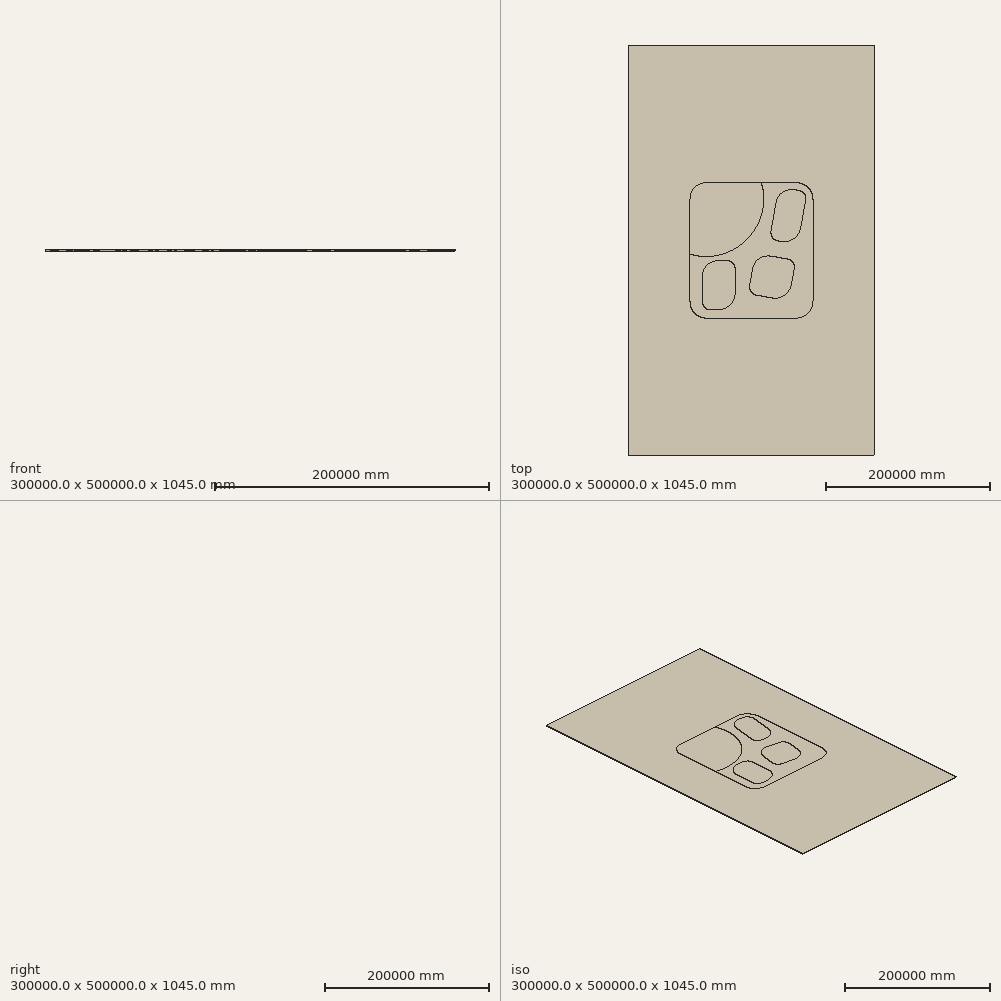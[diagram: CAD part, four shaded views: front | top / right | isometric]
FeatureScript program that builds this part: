
annotation { "Feature Type Name" : "Feature", "Feature Type Description" : "" }
export const myFeature = defineFeature(function(context is Context, id is Id, definition is map)
    precondition{}
    {
        {
            assignVariable(context, id + "F0", {"name" : "building1_height", "anyValue" : 15});
        }
        {
            assignVariable(context, id + "F1", {"name" : "building1_orient", "anyValue" : 0});
        }
        {
            assignVariable(context, id + "F2", {"name" : "building2_height", "anyValue" : 30});
        }
        {
            assignVariable(context, id + "F3", {"name" : "building2_orient", "anyValue" : 10});
        }
        {
            assignVariable(context, id + "F4", {"name" : "building3_height", "anyValue" : 45});
        }
        {
            assignVariable(context, id + "F5", {"name" : "building3_orient", "anyValue" : 10});
        }
        {
            var Q0;
            Q0=qCreatedBy(makeId("Top.planeOp"),FACE);
            var sketch = newSketch(context, id + "F6", { "sketchPlane" : qUnion([Q0])});
            skLineSegment(sketch, "E0.bottom", {"start": v(-55000, 82500) * mm, "end": v(55000, 82500) * mm});
            skLineSegment(sketch, "E0.top", {"start": v(-55000, -82500) * mm, "end": v(55000, -82500) * mm});
            skLineSegment(sketch, "E0.left", {"start": v(-75000, 62500) * mm, "end": v(-75000, -62500) * mm});
            skLineSegment(sketch, "E0.right", {"start": v(75000, 62500) * mm, "end": v(75000, -62500) * mm});
            skPoint(sketch, "E0.middle", {"position": v(0, 0) * mm});
            skLineSegment(sketch, "E1.bottom", {"start": v(-40000, -12500) * mm, "end": v(-30000, -12500) * mm});
            skLineSegment(sketch, "E1.top", {"start": v(-50000, -72500) * mm, "end": v(-40000, -72500) * mm});
            skLineSegment(sketch, "E1.left", {"start": v(-60000, -32500) * mm, "end": v(-60000, -62500) * mm});
            skLineSegment(sketch, "E1.right", {"start": v(-20000, -22500) * mm, "end": v(-20000, -52500) * mm});
            skPoint(sketch, "E1.middle", {"position": v(-40000, -42500) * mm});
            skPoint(sketch, "E1.cornerSnap0", {"position": v(-60000, -47500) * mm});
            skPoint(sketch, "E2.visualSharp", {"position": v(-60000, -12500) * mm});
            skArc(sketch, "E2.filletArc", {"start": v(-40000, -12500) * mm, "mid": v(-54142.14, -18357.86) * mm, "end": v(-60000, -32500) * mm});
            skPoint(sketch, "E3.visualSharp", {"position": v(-20000, -72500) * mm});
            skArc(sketch, "E3.filletArc", {"start": v(-40000, -72500) * mm, "mid": v(-25857.86, -66642.14) * mm, "end": v(-20000, -52500) * mm});
            skPoint(sketch, "E4.visualSharp", {"position": v(-20000, -12500) * mm});
            skArc(sketch, "E4.filletArc", {"start": v(-20000, -22500) * mm, "mid": v(-22928.93, -15428.93) * mm, "end": v(-30000, -12500) * mm});
            skPoint(sketch, "E5.visualSharp", {"position": v(-60000, -72500) * mm});
            skArc(sketch, "E5.filletArc", {"start": v(-60000, -62500) * mm, "mid": v(-57071.07, -69571.07) * mm, "end": v(-50000, -72500) * mm});
            skLineSegment(sketch, "E6.bottom", {"start": v(-75000, -82500) * mm, "end": v(-40000, -82500) * mm, "construction": true});
            skLineSegment(sketch, "E6.top", {"start": v(-75000, -42500) * mm, "end": v(-40000, -42500) * mm, "construction": true});
            skLineSegment(sketch, "E6.left", {"start": v(-75000, -82500) * mm, "end": v(-75000, -42500) * mm, "construction": true});
            skLineSegment(sketch, "E6.right", {"start": v(-40000, -82500) * mm, "end": v(-40000, -42500) * mm, "construction": true});
            skLineSegment(sketch, "E7.bottom", {"start": v(-75000, -82500) * mm, "end": v(25000, -82500) * mm});
            skLineSegment(sketch, "E7.top", {"start": v(-75000, -32500) * mm, "end": v(25000, -32500) * mm, "construction": true});
            skLineSegment(sketch, "E7.left", {"start": v(-75000, -82500) * mm, "end": v(-75000, -32500) * mm});
            skLineSegment(sketch, "E7.right", {"start": v(25000, -82500) * mm, "end": v(25000, -32500) * mm, "construction": true});
            skLineSegment(sketch, "E8.bottom", {"start": v(20000, -7500) * mm, "end": v(40000, -7500) * mm});
            skLineSegment(sketch, "E8.top", {"start": v(10000, -57500) * mm, "end": v(30000, -57500) * mm});
            skLineSegment(sketch, "E8.left", {"start": v(0, -27500) * mm, "end": v(0, -47500) * mm});
            skLineSegment(sketch, "E8.right", {"start": v(50000, -17500) * mm, "end": v(50000, -37500) * mm});
            skPoint(sketch, "E8.middle", {"position": v(25000, -32500) * mm});
            skPoint(sketch, "E9.visualSharp", {"position": v(0, -7500) * mm});
            skArc(sketch, "E9.filletArc", {"start": v(20000, -7500) * mm, "mid": v(5857.86, -13357.86) * mm, "end": v(0, -27500) * mm});
            skPoint(sketch, "E10.visualSharp", {"position": v(50000, -7500) * mm});
            skArc(sketch, "E10.filletArc", {"start": v(50000, -17500) * mm, "mid": v(47071.07, -10428.93) * mm, "end": v(40000, -7500) * mm});
            skPoint(sketch, "E11.visualSharp", {"position": v(50000, -57500) * mm});
            skArc(sketch, "E11.filletArc", {"start": v(30000, -57500) * mm, "mid": v(44142.14, -51642.14) * mm, "end": v(50000, -37500) * mm});
            skPoint(sketch, "E12.visualSharp", {"position": v(0, -57500) * mm});
            skArc(sketch, "E12.filletArc", {"start": v(0, -47500) * mm, "mid": v(2928.93, -54571.07) * mm, "end": v(10000, -57500) * mm});
            skLineSegment(sketch, "E13.bottom", {"start": v(-75000, -82500) * mm, "end": v(45000, -82500) * mm});
            skLineSegment(sketch, "E13.top", {"start": v(-75000, 42500) * mm, "end": v(45000, 42500) * mm, "construction": true});
            skLineSegment(sketch, "E13.left", {"start": v(-75000, -82500) * mm, "end": v(-75000, 42500) * mm});
            skLineSegment(sketch, "E13.right", {"start": v(45000, -82500) * mm, "end": v(45000, 42500) * mm, "construction": true});
            skLineSegment(sketch, "E14.bottom", {"start": v(47500, 75000) * mm, "end": v(52500, 75000) * mm});
            skLineSegment(sketch, "E14.top", {"start": v(37500, 10000) * mm, "end": v(42500, 10000) * mm});
            skLineSegment(sketch, "E14.left", {"start": v(27500, 55000) * mm, "end": v(27500, 20000) * mm});
            skLineSegment(sketch, "E14.right", {"start": v(62500, 65000) * mm, "end": v(62500, 30000) * mm});
            skPoint(sketch, "E14.middle", {"position": v(45000, 42500) * mm});
            skPoint(sketch, "E15.visualSharp", {"position": v(27500, 75000) * mm});
            skArc(sketch, "E15.filletArc", {"start": v(47500, 75000) * mm, "mid": v(33357.86, 69142.14) * mm, "end": v(27500, 55000) * mm});
            skPoint(sketch, "E16.visualSharp", {"position": v(62500, 75000) * mm});
            skArc(sketch, "E16.filletArc", {"start": v(62500, 65000) * mm, "mid": v(59571.07, 72071.07) * mm, "end": v(52500, 75000) * mm});
            skPoint(sketch, "E17.visualSharp", {"position": v(62500, 10000) * mm});
            skArc(sketch, "E17.filletArc", {"start": v(42500, 10000) * mm, "mid": v(56642.14, 15857.86) * mm, "end": v(62500, 30000) * mm});
            skPoint(sketch, "E18.visualSharp", {"position": v(27500, 10000) * mm});
            skArc(sketch, "E18.filletArc", {"start": v(27500, 20000) * mm, "mid": v(30428.93, 12928.93) * mm, "end": v(37500, 10000) * mm});
            skPoint(sketch, "E19.visualSharp", {"position": v(-75000, -82500) * mm});
            skArc(sketch, "E19.filletArc", {"start": v(-75000, -62500) * mm, "mid": v(-69142.14, -76642.14) * mm, "end": v(-55000, -82500) * mm});
            skPoint(sketch, "E20.visualSharp", {"position": v(75000, -82500) * mm});
            skArc(sketch, "E20.filletArc", {"start": v(55000, -82500) * mm, "mid": v(69142.14, -76642.14) * mm, "end": v(75000, -62500) * mm});
            skPoint(sketch, "E21.visualSharp", {"position": v(75000, 82500) * mm});
            skArc(sketch, "E21.filletArc", {"start": v(75000, 62500) * mm, "mid": v(69142.14, 76642.14) * mm, "end": v(55000, 82500) * mm});
            skPoint(sketch, "E22.visualSharp", {"position": v(-75000, 82500) * mm});
            skArc(sketch, "E22.filletArc", {"start": v(-55000, 82500) * mm, "mid": v(-69142.14, 76642.14) * mm, "end": v(-75000, 62500) * mm});
            skArc(sketch, "E23", {"start": v(12082.04, 82500) * mm, "mid": v(-5502.53, 13002.53) * mm, "end": v(-75000, -4582.04) * mm});
            skSolve(sketch);
        }
        {
            var Q0;
            Q0=makeQuery(id+"F6.imprint","IMPRINT",FACE,{"disambiguationData":[TD([[makeQuery(id+"F6.imprint","IMPRINT",EDGE,{"derivedFrom":sQuery(id+"F6.wireOp",EDGE,"E1.bottom")}),-1.0]])]});
            extrude(context, id + "F7", {"entities" : qUnion([Q0]), "depth" : (getVariable(context, 'building1_height')) * mm, "offsetDistance" : 25 * mm});
        }
        {
            var Q0;
            Q0=makeQuery(id+"F6.imprint","IMPRINT",FACE,{"disambiguationData":[TD([[makeQuery(id+"F6.imprint","IMPRINT",EDGE,{"derivedFrom":sQuery(id+"F6.wireOp",EDGE,"E8.bottom")}),-1.0]])]});
            extrude(context, id + "F8", {"entities" : qUnion([Q0]), "depth" : (getVariable(context, 'building2_height')) * mm, "offsetDistance" : 25 * mm});
        }
        {
            var Q0;
            Q0=makeQuery(id+"F6.imprint","IMPRINT",FACE,{"disambiguationData":[TD([[makeQuery(id+"F6.imprint","IMPRINT",EDGE,{"derivedFrom":sQuery(id+"F6.wireOp",EDGE,"E14.bottom")}),-1.0]])]});
            extrude(context, id + "F9", {"entities" : qUnion([Q0]), "depth" : (getVariable(context, 'building3_height')) * mm, "offsetDistance" : 25 * mm});
        }
        {
            var Q0;
            {var subQ1=sQuery(id+"F6.wireOp",EDGE,"E0.top");Q0=makeQuery(id+"F6.imprint","IMPRINT",FACE,{"disambiguationData":[TD([[makeQuery(id+"F6.imprint","IMPRINT",EDGE,{"derivedFrom":subQ1}),1.0]])]});}
            var Q1;
            Q1=makeQuery(id+"F6.imprint","IMPRINT",FACE,{"disambiguationData":[TD([[makeQuery(id+"F6.imprint","IMPRINT",EDGE,{"derivedFrom":sQuery(id+"F6.wireOp",EDGE,"E8.bottom")}),-1.0]])]});
            var Q2;
            Q2=makeQuery(id+"F6.imprint","IMPRINT",FACE,{"disambiguationData":[TD([[makeQuery(id+"F6.imprint","IMPRINT",EDGE,{"derivedFrom":sQuery(id+"F6.wireOp",EDGE,"E14.bottom")}),-1.0]])]});
            var Q3;
            Q3=makeQuery(id+"F6.imprint","IMPRINT",FACE,{"disambiguationData":[TD([[makeQuery(id+"F6.imprint","IMPRINT",EDGE,{"derivedFrom":sQuery(id+"F6.wireOp",EDGE,"E1.bottom")}),-1.0]])]});
            extrude(context, id + "F10", {"entities" : qUnion([Q0, Q1, Q2, Q3]), "oppositeDirection" : true, "depth" : 1000 * mm, "offsetDistance" : 25 * mm});
        }
        {
            var Q0;
            {var subQ1=sQuery(id+"F6.wireOp",EDGE,"E0.left");Q0=makeQuery(id+"F6.imprint","IMPRINT",FACE,{"disambiguationData":[TD([[makeQuery(id+"F6.imprint","IMPRINT",EDGE,{"derivedFrom":subQ1}),1.0]])]});}
            extrude(context, id + "F11", {"entities" : qUnion([Q0]), "oppositeDirection" : true, "depth" : 1000 * mm, "offsetDistance" : 25 * mm});
        }
        {
            var Q0;
            Q0=sQuery(id+"F6.wireOp",EDGE,"E6.top");
            cPlane(context, id + "F12", {"entities" : qUnion([Q0]), "cplaneType" : CPlaneType.LINE_ANGLE, "offset" : 25 * mm, "angle" : 0 * degree, "width" : 150 * mm, "height" : 150 * mm});
        }
        {
            var Q0;
            Q0=sQuery(id+"F6.wireOp",EDGE,"E7.top");
            cPlane(context, id + "F13", {"entities" : qUnion([Q0]), "cplaneType" : CPlaneType.LINE_ANGLE, "offset" : 25 * mm, "angle" : 0 * degree, "width" : 150 * mm, "height" : 150 * mm});
        }
        {
            var Q0;
            Q0=sQuery(id+"F6.wireOp",EDGE,"E13.top");
            cPlane(context, id + "F14", {"entities" : qUnion([Q0]), "cplaneType" : CPlaneType.LINE_ANGLE, "offset" : 25 * mm, "angle" : 0 * degree, "width" : 150 * mm, "height" : 150 * mm});
        }
        {
            var Q0;
            Q0=qCreatedBy(id+"F12.planeOp",FACE);
            var sketch = newSketch(context, id + "F15", { "sketchPlane" : qUnion([Q0])});
            skLineSegment(sketch, "E24", {"start": v(40000, 0) * mm, "end": v(40000, 15000) * mm});
            skSolve(sketch);
        }
        {
            var Q0;
            Q0=qCreatedBy(id+"F13.planeOp",FACE);
            var sketch = newSketch(context, id + "F16", { "sketchPlane" : qUnion([Q0])});
            skLineSegment(sketch, "E25", {"start": v(-25000, 0) * mm, "end": v(-25000, 30000) * mm});
            skSolve(sketch);
        }
        {
            var Q0;
            Q0=qCreatedBy(id+"F14.planeOp",FACE);
            var sketch = newSketch(context, id + "F17", { "sketchPlane" : qUnion([Q0])});
            skLineSegment(sketch, "E26", {"start": v(-45000, 0) * mm, "end": v(-45000, 45000) * mm});
            skSolve(sketch);
        }
        {
            var Q0;
            Q0=makeQuery(id+"F7.opExtrude","SWEPT_BODY",BODY,{"disambiguationData":[OSD([sQuery(id+"F6.wireOp",EDGE,"E1.bottom"),sQuery(id+"F6.wireOp",EDGE,"E1.top"),sQuery(id+"F6.wireOp",EDGE,"E1.left"),sQuery(id+"F6.wireOp",EDGE,"E1.right"),sQuery(id+"F6.wireOp",EDGE,"E2.filletArc"),sQuery(id+"F6.wireOp",EDGE,"E3.filletArc"),sQuery(id+"F6.wireOp",EDGE,"E4.filletArc"),sQuery(id+"F6.wireOp",EDGE,"E5.filletArc")])]});
            var Q1;
            Q1=sQuery(id+"F15.wireOp",EDGE,"E24");
            transform(context, id + "F18", {"entities" : qUnion([Q0]), "transformType" : TransformType.ROTATION, "transformAxis" : qUnion([Q1]), "angle" : (getVariable(context, 'building1_orient')) * degree, "oppositeDirection" : true, "makeCopy" : false});
        }
        {
            var Q0;
            Q0=makeQuery(id+"F8.opExtrude","SWEPT_BODY",BODY,{"disambiguationData":[OSD([sQuery(id+"F6.wireOp",EDGE,"E8.bottom"),sQuery(id+"F6.wireOp",EDGE,"E8.top"),sQuery(id+"F6.wireOp",EDGE,"E8.left"),sQuery(id+"F6.wireOp",EDGE,"E8.right"),sQuery(id+"F6.wireOp",EDGE,"E9.filletArc"),sQuery(id+"F6.wireOp",EDGE,"E10.filletArc"),sQuery(id+"F6.wireOp",EDGE,"E11.filletArc"),sQuery(id+"F6.wireOp",EDGE,"E12.filletArc")])]});
            var Q1;
            Q1=sQuery(id+"F16.wireOp",EDGE,"E25");
            transform(context, id + "F19", {"entities" : qUnion([Q0]), "transformType" : TransformType.ROTATION, "transformAxis" : qUnion([Q1]), "angle" : (getVariable(context, 'building2_orient')) * degree, "oppositeDirection" : true, "makeCopy" : false});
        }
        {
            var Q0;
            Q0=makeQuery(id+"F9.opExtrude","SWEPT_BODY",BODY,{"disambiguationData":[OSD([sQuery(id+"F6.wireOp",EDGE,"E14.bottom"),sQuery(id+"F6.wireOp",EDGE,"E14.top"),sQuery(id+"F6.wireOp",EDGE,"E14.left"),sQuery(id+"F6.wireOp",EDGE,"E14.right"),sQuery(id+"F6.wireOp",EDGE,"E15.filletArc"),sQuery(id+"F6.wireOp",EDGE,"E16.filletArc"),sQuery(id+"F6.wireOp",EDGE,"E17.filletArc"),sQuery(id+"F6.wireOp",EDGE,"E18.filletArc")])]});
            var Q1;
            Q1=sQuery(id+"F17.wireOp",EDGE,"E26");
            transform(context, id + "F20", {"entities" : qUnion([Q0]), "transformType" : TransformType.ROTATION, "transformAxis" : qUnion([Q1]), "angle" : (getVariable(context, 'building3_orient')) * degree, "oppositeDirection" : true, "makeCopy" : false});
        }
        {
            assignVariable(context, id + "F21", {"name" : "domain_length", "anyValue" : 500});
        }
        {
            assignVariable(context, id + "F22", {"name" : "domain_height", "anyValue" : 200});
        }
        {
            assignVariable(context, id + "F23", {"name" : "domain_length_margin", "anyValue" : 0.25});
        }
        {
            assignVariable(context, id + "F24", {"name" : "domain_orient", "anyValue" : 0});
        }
        {
            var Q0;
            Q0=makeQuery(id+"F10.opExtrude","CAP_FACE",FACE,{"disambiguationData":[OSD([sQuery(id+"F6.wireOp",EDGE,"E0.bottom"),sQuery(id+"F6.wireOp",EDGE,"E0.top"),sQuery(id+"F6.wireOp",EDGE,"E0.right"),sQuery(id+"F6.wireOp",EDGE,"E13.bottom"),sQuery(id+"F6.wireOp",EDGE,"E13.left"),sQuery(id+"F6.wireOp",EDGE,"E19.filletArc"),sQuery(id+"F6.wireOp",EDGE,"E20.filletArc"),sQuery(id+"F6.wireOp",EDGE,"E21.filletArc"),sQuery(id+"F6.wireOp",EDGE,"E23")])],"isStart":false});
            var sketch = newSketch(context, id + "F25", { "sketchPlane" : qUnion([Q0])});
            skLineSegment(sketch, "E27.bottom", {"start": v(-150000, 250000) * mm, "end": v(150000, 250000) * mm});
            skLineSegment(sketch, "E27.top", {"start": v(-150000, -250000) * mm, "end": v(150000, -250000) * mm});
            skLineSegment(sketch, "E27.left", {"start": v(-150000, 250000) * mm, "end": v(-150000, -250000) * mm});
            skLineSegment(sketch, "E27.right", {"start": v(150000, 250000) * mm, "end": v(150000, -250000) * mm});
            skPoint(sketch, "E27.middle", {"position": v(0, 0) * mm});
            skSolve(sketch);
        }
        {
            var Q0;
            Q0=makeQuery(id+"F25.imprint","IMPRINT",FACE,{"disambiguationData":[TD([[makeQuery(id+"F25.imprint","IMPRINT",EDGE,{"derivedFrom":sQuery(id+"F25.wireOp",EDGE,"E27.bottom")}),-1.0]])]});
            var Q1;
            Q1=makeQuery(id+"F25.imprint","IMPRINT",FACE,{"disambiguationData":[TD([[makeQuery(id+"F25.imprint","IMPRINT",EDGE,{"derivedFrom":makeQuery(id+"F10.opExtrude","CAP_EDGE",EDGE,{"disambiguationData":[OSD([sQuery(id+"F6.wireOp",EDGE,"E0.bottom")])],"isStart":false})}),1.0]])]});
            extrude(context, id + "F26", {"entities" : qUnion([Q0, Q1]), "oppositeDirection" : true, "depth" : (getVariable(context, 'domain_height')) * mm, "offsetDistance" : 25 * mm});
        }
        {
            var Q0;
            Q0=makeQuery(id+"F26.opExtrude","SWEPT_BODY",BODY,{"disambiguationData":[OSD([sQuery(id+"F25.wireOp",EDGE,"E27.bottom"),sQuery(id+"F25.wireOp",EDGE,"E27.top"),sQuery(id+"F25.wireOp",EDGE,"E27.left"),sQuery(id+"F25.wireOp",EDGE,"E27.right")])]});
            var Q1;
            Q1=makeQuery(id+"F26.opExtrude","CAP_EDGE",EDGE,{"disambiguationData":[OSD([sQuery(id+"F25.wireOp",EDGE,"E27.left")])],"isStart":true});
            var Q2;
            Q2=makeQuery(id+"F26.opExtrude","SWEPT_FACE",FACE,{"disambiguationData":[OSD([sQuery(id+"F25.wireOp",EDGE,"E27.bottom")])]});
            transform(context, id + "F27", {"entities" : qUnion([Q0]), "transformType" : TransformType.TRANSLATION_DISTANCE, "transformDirection" : qUnion([Q2]), "distance" : (getVariable(context, 'domain_length_margin') * (getVariable(context, 'domain_length') / 2)) * mm, "makeCopy" : false});
        }
        {
            var Q0;
            Q0=qCreatedBy(makeId("Front.planeOp"),FACE);
            var sketch = newSketch(context, id + "F28", { "sketchPlane" : qUnion([Q0])});
            skLineSegment(sketch, "E28", {"start": v(0, 0) * mm, "end": v(0, 1000) * mm, "construction": true});
            skSolve(sketch);
        }
        {
            var Q0;
            Q0=makeQuery(id+"F11.opExtrude","SWEPT_BODY",BODY,{"disambiguationData":[OSD([sQuery(id+"F6.wireOp",EDGE,"E0.bottom"),sQuery(id+"F6.wireOp",EDGE,"E0.left"),sQuery(id+"F6.wireOp",EDGE,"E13.left"),sQuery(id+"F6.wireOp",EDGE,"E22.filletArc"),sQuery(id+"F6.wireOp",EDGE,"E23")])]});
            var Q1;
            Q1=makeQuery(id+"F10.opExtrude","SWEPT_BODY",BODY,{"disambiguationData":[OSD([sQuery(id+"F6.wireOp",EDGE,"E0.bottom"),sQuery(id+"F6.wireOp",EDGE,"E0.top"),sQuery(id+"F6.wireOp",EDGE,"E0.right"),sQuery(id+"F6.wireOp",EDGE,"E13.bottom"),sQuery(id+"F6.wireOp",EDGE,"E13.left"),sQuery(id+"F6.wireOp",EDGE,"E19.filletArc"),sQuery(id+"F6.wireOp",EDGE,"E20.filletArc"),sQuery(id+"F6.wireOp",EDGE,"E21.filletArc"),sQuery(id+"F6.wireOp",EDGE,"E23")])]});
            var Q2;
            Q2=makeQuery(id+"F9.opExtrude","SWEPT_BODY",BODY,{"disambiguationData":[OSD([sQuery(id+"F6.wireOp",EDGE,"E14.bottom"),sQuery(id+"F6.wireOp",EDGE,"E14.top"),sQuery(id+"F6.wireOp",EDGE,"E14.left"),sQuery(id+"F6.wireOp",EDGE,"E14.right"),sQuery(id+"F6.wireOp",EDGE,"E15.filletArc"),sQuery(id+"F6.wireOp",EDGE,"E16.filletArc"),sQuery(id+"F6.wireOp",EDGE,"E17.filletArc"),sQuery(id+"F6.wireOp",EDGE,"E18.filletArc")])]});
            var Q3;
            Q3=makeQuery(id+"F8.opExtrude","SWEPT_BODY",BODY,{"disambiguationData":[OSD([sQuery(id+"F6.wireOp",EDGE,"E8.bottom"),sQuery(id+"F6.wireOp",EDGE,"E8.top"),sQuery(id+"F6.wireOp",EDGE,"E8.left"),sQuery(id+"F6.wireOp",EDGE,"E8.right"),sQuery(id+"F6.wireOp",EDGE,"E9.filletArc"),sQuery(id+"F6.wireOp",EDGE,"E10.filletArc"),sQuery(id+"F6.wireOp",EDGE,"E11.filletArc"),sQuery(id+"F6.wireOp",EDGE,"E12.filletArc")])]});
            var Q4;
            Q4=makeQuery(id+"F7.opExtrude","SWEPT_BODY",BODY,{"disambiguationData":[OSD([sQuery(id+"F6.wireOp",EDGE,"E1.bottom"),sQuery(id+"F6.wireOp",EDGE,"E1.top"),sQuery(id+"F6.wireOp",EDGE,"E1.left"),sQuery(id+"F6.wireOp",EDGE,"E1.right"),sQuery(id+"F6.wireOp",EDGE,"E2.filletArc"),sQuery(id+"F6.wireOp",EDGE,"E3.filletArc"),sQuery(id+"F6.wireOp",EDGE,"E4.filletArc"),sQuery(id+"F6.wireOp",EDGE,"E5.filletArc")])]});
            var Q5;
            Q5=sQuery(id+"F28.wireOp",EDGE,"E28");
            transform(context, id + "F29", {"entities" : qUnion([Q0, Q1, Q2, Q3, Q4]), "transformType" : TransformType.ROTATION, "transformAxis" : qUnion([Q5]), "angle" : (getVariable(context, 'domain_orient')) * degree, "makeCopy" : false});
        }
        {
            var Q0;
            Q0=makeQuery(id+"F26.opExtrude","SWEPT_FACE",FACE,{"disambiguationData":[OSD([sQuery(id+"F25.wireOp",EDGE,"E27.bottom")])]});
            extrude(context, id + "F30", {"entities" : qUnion([Q0]), "oppositeDirection" : true, "depth" : 1000 * mm, "offsetDistance" : 25 * mm});
        }
        {
            var Q0;
            Q0=makeQuery(id+"F26.opExtrude","SWEPT_FACE",FACE,{"disambiguationData":[OSD([sQuery(id+"F25.wireOp",EDGE,"E27.top")])]});
            extrude(context, id + "F31", {"entities" : qUnion([Q0]), "oppositeDirection" : true, "depth" : 1000 * mm, "offsetDistance" : 25 * mm});
        }
        {
            var Q0;
            Q0=makeQuery(id+"F26.opExtrude","CAP_FACE",FACE,{"disambiguationData":[OSD([sQuery(id+"F25.wireOp",EDGE,"E27.bottom"),sQuery(id+"F25.wireOp",EDGE,"E27.top"),sQuery(id+"F25.wireOp",EDGE,"E27.left"),sQuery(id+"F25.wireOp",EDGE,"E27.right")])],"isStart":true});
            extrude(context, id + "F32", {"entities" : qUnion([Q0]), "oppositeDirection" : true, "depth" : 990 * mm, "offsetDistance" : 25 * mm});
        }
    });
